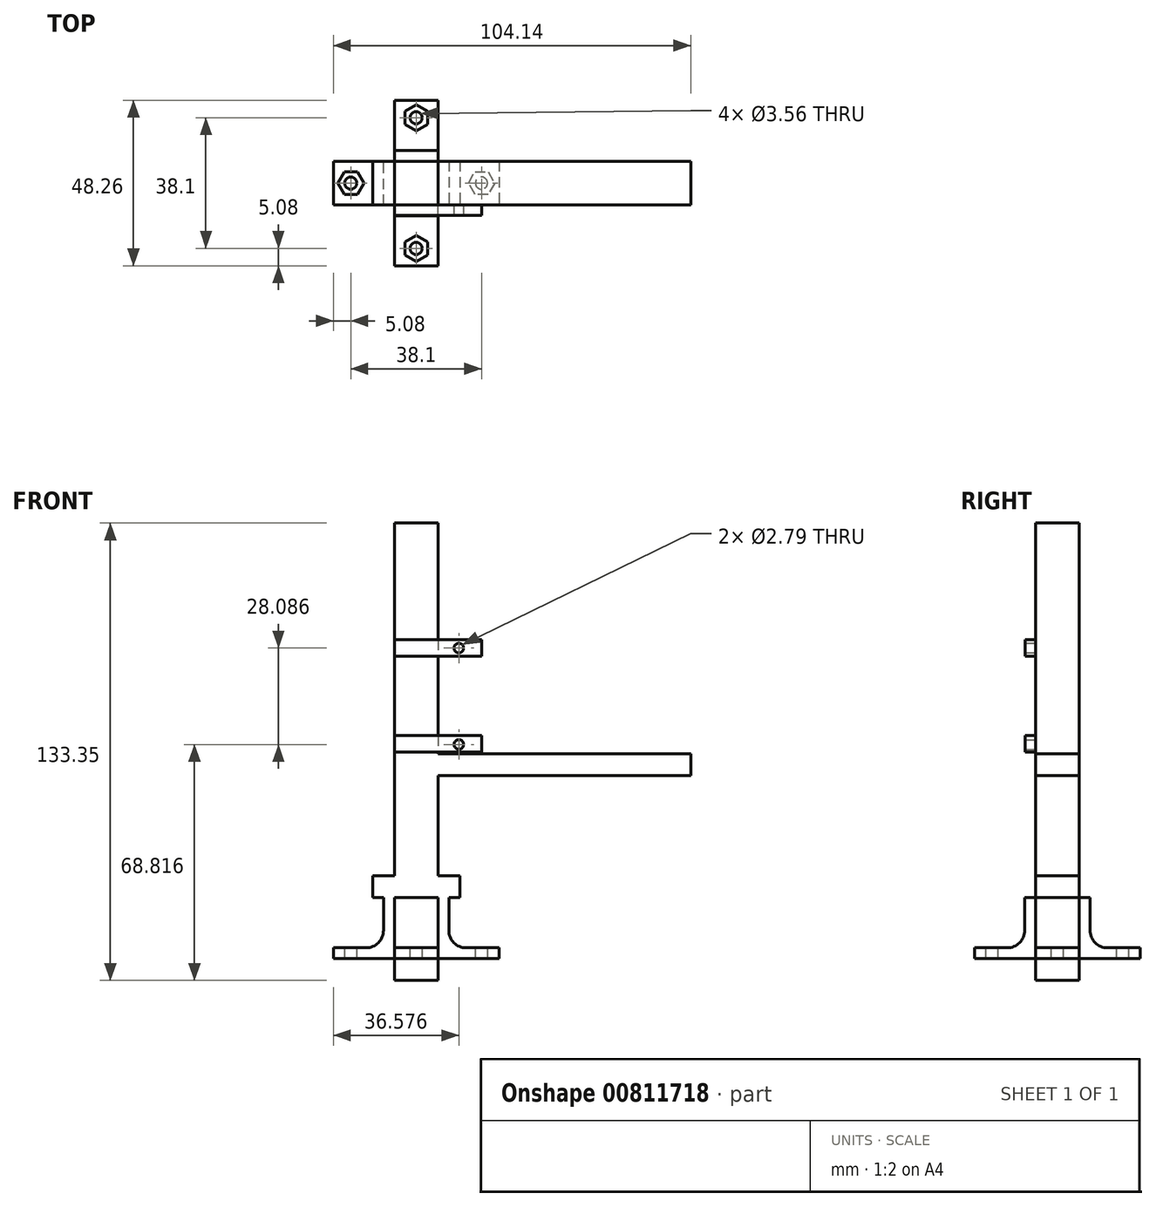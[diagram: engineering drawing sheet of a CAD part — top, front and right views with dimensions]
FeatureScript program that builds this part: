
annotation { "Feature Type Name" : "Feature", "Feature Type Description" : "" }
export const myFeature = defineFeature(function(context is Context, id is Id, definition is map)
    precondition{}
    {
        {
            var Q0;
            Q0=qCreatedBy(makeId("Top.planeOp"),FACE);
            var sketch = newSketch(context, id + "F0", { "sketchPlane" : qUnion([Q0])});
            skLineSegment(sketch, "E0.bottom", {"start": v(6.35, 6.35) * mm, "end": v(-6.35, 6.35) * mm});
            skLineSegment(sketch, "E0.top", {"start": v(6.35, -6.35) * mm, "end": v(-6.35, -6.35) * mm});
            skLineSegment(sketch, "E0.left", {"start": v(6.35, 6.35) * mm, "end": v(6.35, -6.35) * mm});
            skLineSegment(sketch, "E0.right", {"start": v(-6.35, 6.35) * mm, "end": v(-6.35, -6.35) * mm});
            skPoint(sketch, "E0.middle", {"position": v(0, 0) * mm});
            skSolve(sketch);
        }
        {
            var Q0;
            Q0 = qSketchRegion(id + "F0", true);
            extrude(context, id + "F1", {"entities" : qUnion([Q0]), "depth" : 127 * mm, "offsetDistance" : 25.4 * mm});
        }
        {
            var Q0;
            Q0=makeQuery(id+"F1.opExtrude","SWEPT_FACE",FACE,{"disambiguationData":[OSD([sQuery(id+"F0.wireOp",EDGE,"E0.top")])]});
            var sketch = newSketch(context, id + "F2", { "sketchPlane" : qUnion([Q0])});
            skLineSegment(sketch, "E1", {"start": v(6.35, 0) * mm, "end": v(24.13, 0) * mm});
            skLineSegment(sketch, "E2", {"start": v(24.13, 0) * mm, "end": v(24.13, 3.17) * mm});
            skLineSegment(sketch, "E3", {"start": v(24.13, 3.18) * mm, "end": v(14.6, 3.17) * mm});
            skLineSegment(sketch, "E4", {"start": v(9.53, 8.26) * mm, "end": v(9.53, 17.78) * mm});
            skLineSegment(sketch, "E5", {"start": v(9.53, 17.78) * mm, "end": v(6.35, 17.78) * mm});
            skPoint(sketch, "E6.visualSharp", {"position": v(9.53, 3.17) * mm});
            skArc(sketch, "E6.filletArc", {"start": v(9.53, 8.26) * mm, "mid": v(11.01, 4.66) * mm, "end": v(14.6, 3.18) * mm});
            skLineSegment(sketch, "E7", {"start": v(6.35, 17.78) * mm, "end": v(6.35, 0) * mm});
            skSolve(sketch);
        }
        {
            var Q0;
            Q0 = qSketchRegion(id + "F2", true);
            extrude(context, id + "F3", {"entities" : qUnion([Q0]), "oppositeDirection" : true, "depth" : 12.7 * mm, "offsetDistance" : 25.4 * mm});
        }
        {
            var Q0;
            Q0=makeQuery(id+"F3.opExtrude","SWEPT_FACE",FACE,{"disambiguationData":[OSD([sQuery(id+"F2.wireOp",EDGE,"E3")])]});
            var sketch = newSketch(context, id + "F4", { "sketchPlane" : qUnion([Q0])});
            skLineSegment(sketch, "E8", {"start": v(6.35, 0) * mm, "end": v(19.05, 0) * mm});
            skCircle(sketch, "E9", {"center": v(19.05, 0) * mm, "radius": 1.78 * mm});
            skCircle(sketch, "E10", {"center": v(19.05, 0) * mm, "radius": 3.3 * mm});
            skCircle(sketch, "E11.cCircle", {"center": v(19.05, 0) * mm, "radius": 3.3 * mm, "construction": true});
            skLineSegment(sketch, "E11.0", {"start": v(17.14, 3.3) * mm, "end": v(20.96, 3.3) * mm});
            skLineSegment(sketch, "E11.1", {"start": v(20.96, 3.3) * mm, "end": v(22.86, 0) * mm});
            skLineSegment(sketch, "E11.2", {"start": v(22.86, 0) * mm, "end": v(20.96, -3.3) * mm});
            skLineSegment(sketch, "E11.3", {"start": v(20.96, -3.3) * mm, "end": v(17.14, -3.3) * mm});
            skLineSegment(sketch, "E11.4", {"start": v(17.14, -3.3) * mm, "end": v(15.24, 0) * mm});
            skLineSegment(sketch, "E11.5", {"start": v(15.24, 0) * mm, "end": v(17.14, 3.3) * mm});
            skPoint(sketch, "E11.0.midPoint", {"position": v(19.05, 3.3) * mm});
            skSolve(sketch);
        }
        {
            var Q0;
            Q0 = qSketchRegion(id + "F4", true);
            extrude(context, id + "F5", {"entities" : qUnion([Q0]), "operationType" : NewBodyOperationType.REMOVE, "oppositeDirection" : true, "depth" : 3 / 812.8 * mm, "offsetDistance" : 25.4 * mm});
        }
        {
            var Q0;
            Q0=makeQuery(id+"F4.imprint","IMPRINT",FACE,{"disambiguationData":[TD([[makeQuery(id+"F4.imprint","IMPRINT",EDGE,{"derivedFrom":sQuery(id+"F4.wireOp",EDGE,"E9")}),1.0]])]});
            extrude(context, id + "F6", {"entities" : qUnion([Q0]), "operationType" : NewBodyOperationType.REMOVE, "oppositeDirection" : true, "depth" : 25.4 * mm, "offsetDistance" : 25.4 * mm});
        }
        {
            var Q0;
            Q0=qCreatedBy(makeId("Front.planeOp"),FACE);
            var sketch = newSketch(context, id + "F7", { "sketchPlane" : qUnion([Q0])});
            skLineSegment(sketch, "E12", {"start": v(0, 129.56) * mm, "end": v(0, -46.45) * mm, "construction": true});
            skSolve(sketch);
        }
        {
            var Q0;
            Q0=makeQuery(id+"F3.opExtrude","SWEPT_BODY",BODY,{"disambiguationData":[OSD([sQuery(id+"F2.wireOp",EDGE,"E1"),sQuery(id+"F2.wireOp",EDGE,"E2"),sQuery(id+"F2.wireOp",EDGE,"E3"),sQuery(id+"F2.wireOp",EDGE,"E4"),sQuery(id+"F2.wireOp",EDGE,"E5"),sQuery(id+"F2.wireOp",EDGE,"E6.filletArc"),sQuery(id+"F2.wireOp",EDGE,"E7")])]});
            var Q1;
            Q1=sQuery(id+"F7.wireOp",EDGE,"E12");
            circularPattern(context, id + "F8", {"entities" : qUnion([Q0]), "axis" : qUnion([Q1]), "angle" : 360 * degree, "instanceCount" : 4, "equalSpace" : true});
        }
        {
            var Q0;
            Q0 = qSketchRegion(id + "F0", true);
            extrude(context, id + "F9", {"entities" : qUnion([Q0]), "operationType" : NewBodyOperationType.ADD, "oppositeDirection" : true, "depth" : 6.35 * mm, "offsetDistance" : 25.4 * mm});
        }
        {
            var Q0;
            {var subQ0=sQuery(id+"F0.wireOp",EDGE,"E0.top");Q0=makeQuery(id+"F9.boolean.opBoolean","MERGE",FACE,{"derivedFrom":[makeQuery(id+"F1.opExtrude","SWEPT_FACE",FACE,{"disambiguationData":[OSD([subQ0])]}),makeQuery(id+"F9.opExtrude","SWEPT_FACE",FACE,{"disambiguationData":[OSD([subQ0])]})]});}
            var sketch = newSketch(context, id + "F10", { "sketchPlane" : qUnion([Q0])});
            skLineSegment(sketch, "E13", {"start": v(6.35, 0) * mm, "end": v(6.35, 53.34) * mm});
            skLineSegment(sketch, "E14", {"start": v(6.35, 53.34) * mm, "end": v(80.01, 53.34) * mm});
            skLineSegment(sketch, "E15", {"start": v(6.35, 53.34) * mm, "end": v(6.35, 59.69) * mm});
            skLineSegment(sketch, "E16", {"start": v(6.35, 59.69) * mm, "end": v(80.01, 59.69) * mm});
            skLineSegment(sketch, "E17", {"start": v(80.01, 53.34) * mm, "end": v(80.01, 59.69) * mm});
            skSolve(sketch);
        }
        {
            var Q0;
            Q0=makeQuery(id+"F10.imprint","IMPRINT",FACE,{"disambiguationData":[TD([[makeQuery(id+"F10.imprint","IMPRINT",EDGE,{"derivedFrom":sQuery(id+"F10.wireOp",EDGE,"E14")}),1.0]])]});
            extrude(context, id + "F11", {"entities" : qUnion([Q0]), "operationType" : NewBodyOperationType.ADD, "oppositeDirection" : true, "depth" : 12.7 * mm, "offsetDistance" : 25.4 * mm});
        }
        {
            var Q0;
            {var subQ0=sQuery(id+"F0.wireOp",EDGE,"E0.top");Q0=makeQuery(id+"F11.boolean.opBoolean","MERGE",FACE,{"derivedFrom":[makeQuery(id+"F9.boolean.opBoolean","MERGE",FACE,{"derivedFrom":[makeQuery(id+"F1.opExtrude","SWEPT_FACE",FACE,{"disambiguationData":[OSD([subQ0])]}),makeQuery(id+"F9.opExtrude","SWEPT_FACE",FACE,{"disambiguationData":[OSD([subQ0])]})]}),makeQuery(id+"F11.opExtrude","CAP_FACE",FACE,{"disambiguationData":[OSD([sQuery(id+"F10.wireOp",EDGE,"E14"),sQuery(id+"F10.wireOp",EDGE,"E15"),sQuery(id+"F10.wireOp",EDGE,"E16"),sQuery(id+"F10.wireOp",EDGE,"E17")])],"isStart":true})]});}
            var sketch = newSketch(context, id + "F12", { "sketchPlane" : qUnion([Q0])});
            skLineSegment(sketch, "E18", {"start": v(6.35, 17.78) * mm, "end": v(12.7, 17.78) * mm});
            skLineSegment(sketch, "E19", {"start": v(12.7, 17.78) * mm, "end": v(12.7, 24.13) * mm});
            skLineSegment(sketch, "E20", {"start": v(12.7, 24.13) * mm, "end": v(6.35, 24.13) * mm});
            skLineSegment(sketch, "E21", {"start": v(6.35, 17.78) * mm, "end": v(6.35, 24.13) * mm});
            skLineSegment(sketch, "E22.MirrorCS", {"start": v(-12.7, 17.78) * mm, "end": v(-12.7, 24.13) * mm});
            skLineSegment(sketch, "E23.MirrorCS", {"start": v(-6.35, 17.78) * mm, "end": v(-12.7, 17.78) * mm});
            skLineSegment(sketch, "E24.MirrorCS", {"start": v(-6.35, 17.78) * mm, "end": v(-6.35, 24.13) * mm});
            skLineSegment(sketch, "E25.MirrorCS", {"start": v(-12.7, 24.13) * mm, "end": v(-6.35, 24.13) * mm});
            skSolve(sketch);
        }
        {
            var Q0;
            Q0 = qSketchRegion(id + "F12", true);
            var Q1;
            Q1=makeQuery(id+"F12.imprint","IMPRINT",FACE,{"disambiguationData":[TD([[makeQuery(id+"F12.imprint","IMPRINT",EDGE,{"derivedFrom":sQuery(id+"F12.wireOp",EDGE,"E18")}),1.0]])]});
            extrude(context, id + "F13", {"entities" : qUnion([Q0, Q1]), "operationType" : NewBodyOperationType.ADD, "oppositeDirection" : true, "depth" : 12.7 * mm, "offsetDistance" : 25.4 * mm});
        }
        {
            var Q0;
            {var subQ0=sQuery(id+"F0.wireOp",EDGE,"E0.top");Q0=makeQuery(id+"F11.boolean.opBoolean","MERGE",FACE,{"derivedFrom":[makeQuery(id+"F9.boolean.opBoolean","MERGE",FACE,{"derivedFrom":[makeQuery(id+"F1.opExtrude","SWEPT_FACE",FACE,{"disambiguationData":[OSD([subQ0])]}),makeQuery(id+"F9.opExtrude","SWEPT_FACE",FACE,{"disambiguationData":[OSD([subQ0])]})]}),makeQuery(id+"F11.opExtrude","CAP_FACE",FACE,{"disambiguationData":[OSD([sQuery(id+"F10.wireOp",EDGE,"E14"),sQuery(id+"F10.wireOp",EDGE,"E15"),sQuery(id+"F10.wireOp",EDGE,"E16"),sQuery(id+"F10.wireOp",EDGE,"E17")])],"isStart":true})]});}
            var sketch = newSketch(context, id + "F14", { "sketchPlane" : qUnion([Q0])});
            skLineSegment(sketch, "E26", {"start": v(6.35, 60.2) * mm, "end": v(19.05, 60.2) * mm});
            skLineSegment(sketch, "E27", {"start": v(6.35, 60.2) * mm, "end": v(-6.35, 60.2) * mm});
            skLineSegment(sketch, "E28", {"start": v(19.05, 60.2) * mm, "end": v(19.05, 65.02) * mm});
            skLineSegment(sketch, "E29", {"start": v(6.35, 65.02) * mm, "end": v(19.05, 65.02) * mm});
            skLineSegment(sketch, "E30", {"start": v(11.05, 62.47) * mm, "end": v(12.45, 62.47) * mm});
            skLineSegment(sketch, "E31", {"start": v(6.35, 88.14) * mm, "end": v(19.05, 88.14) * mm});
            skLineSegment(sketch, "E32", {"start": v(19.05, 88.14) * mm, "end": v(19.05, 92.96) * mm});
            skLineSegment(sketch, "E33", {"start": v(19.05, 92.96) * mm, "end": v(6.35, 92.96) * mm});
            skLineSegment(sketch, "E34", {"start": v(11.05, 90.55) * mm, "end": v(12.45, 90.55) * mm});
            skCircle(sketch, "E35", {"center": v(12.45, 90.55) * mm, "radius": 1.4 * mm});
            skCircle(sketch, "E36", {"center": v(12.45, 62.47) * mm, "radius": 1.4 * mm});
            skLineSegment(sketch, "E37", {"start": v(6.35, 88.14) * mm, "end": v(-6.35, 88.14) * mm});
            skLineSegment(sketch, "E38", {"start": v(-6.35, 88.14) * mm, "end": v(-6.35, 92.96) * mm});
            skLineSegment(sketch, "E39", {"start": v(-6.35, 92.96) * mm, "end": v(6.35, 92.96) * mm});
            skPoint(sketch, "E40.orphan", {"position": v(6.35, 90.55) * mm});
            skLineSegment(sketch, "E41", {"start": v(6.35, 65.02) * mm, "end": v(-6.35, 65.02) * mm});
            skLineSegment(sketch, "E42", {"start": v(-6.35, 65.02) * mm, "end": v(-6.35, 60.2) * mm});
            skPoint(sketch, "E43.end.orphan", {"position": v(6.35, 62.47) * mm});
            skLineSegment(sketch, "E44", {"start": v(6.35, 62.47) * mm, "end": v(12.45, 62.47) * mm});
            skSolve(sketch);
        }
        {
            var Q0;
            Q0 = qSketchRegion(id + "F14", true);
            extrude(context, id + "F15", {"entities" : qUnion([Q0]), "operationType" : NewBodyOperationType.ADD, "depth" : 3.05 * mm, "offsetDistance" : 25.4 * mm});
        }
    });
